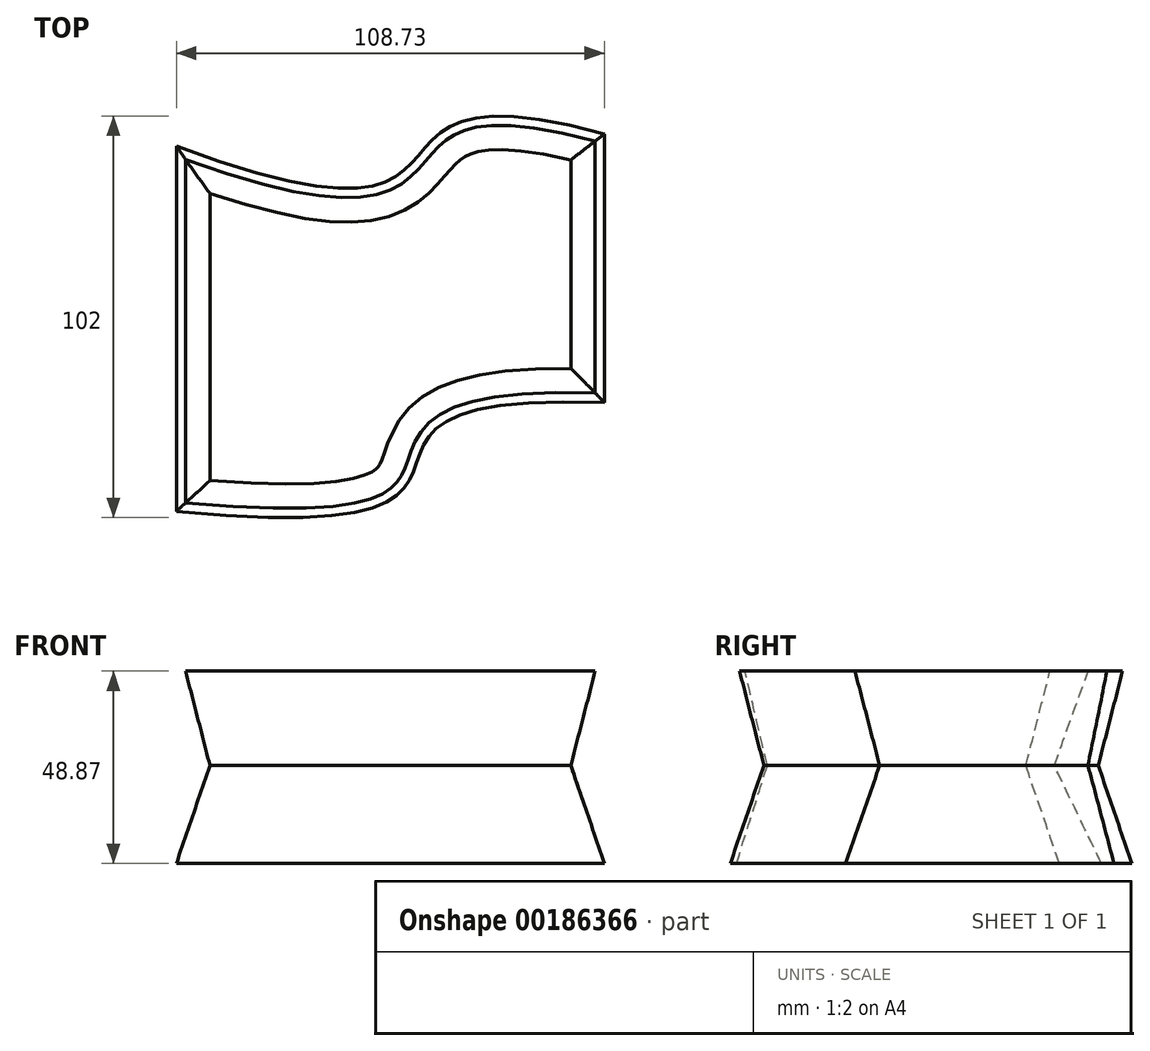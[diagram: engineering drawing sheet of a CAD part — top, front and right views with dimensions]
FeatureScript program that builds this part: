
annotation { "Feature Type Name" : "Feature", "Feature Type Description" : "" }
export const myFeature = defineFeature(function(context is Context, id is Id, definition is map)
    precondition{}
    {
        {
            var Q0;
            Q0=qCreatedBy(makeId("Top.planeOp"),FACE);
            var sketch = newSketch(context, id + "F0", { "sketchPlane" : qUnion([Q0])});
            skLineSegment(sketch, "E0", {"start": v(62.62, 42.09) * mm, "end": v(62.62, -26.14) * mm});
            skLineSegment(sketch, "E1", {"start": v(-46.11, 38.97) * mm, "end": v(-46.11, 0) * mm});
            skFitSpline(sketch, "E2", {"points": [v(62.62, 42.09) * mm, v(-46.11, 38.97) * mm], "startDerivative": vector(-221.63, 61.3) * mm, "endDerivative": vector(-271.64, 100.05) * mm});
            skFitSpline(sketch, "E3", {"points": [v(62.62, -26.14) * mm, v(-46.11, -53.77) * mm], "startDerivative": vector(-264.1, 9.7) * mm, "endDerivative": vector(-314.42, 30.05) * mm});
            skLineSegment(sketch, "E4", {"start": v(-46.11, 0) * mm, "end": v(-46.11, -53.77) * mm});
            skSolve(sketch);
        }
        {
            var Q0;
            Q0=qCreatedBy(makeId("Front.planeOp"),FACE);
            var sketch = newSketch(context, id + "F1", { "sketchPlane" : qUnion([Q0])});
            skLineSegment(sketch, "E5", {"start": v(-46.11, 0) * mm, "end": v(0, 0) * mm});
            skLineSegment(sketch, "E6", {"start": v(0, 0) * mm, "end": v(0, 48.87) * mm});
            skLineSegment(sketch, "E7", {"start": v(0, 48.87) * mm, "end": v(-43.77, 48.87) * mm});
            skLineSegment(sketch, "E8", {"start": v(-43.77, 48.87) * mm, "end": v(-37.59, 24.89) * mm});
            skLineSegment(sketch, "E9", {"start": v(-37.59, 24.89) * mm, "end": v(-46.11, 0) * mm});
            skSolve(sketch);
        }
        {
            var Q0;
            Q0 = qSketchRegion(id + "F1", true);
            var Q1;
            Q1=sQuery(id+"F1.wireOp",EDGE,"E8");
            var Q2;
            Q2=sQuery(id+"F1.wireOp",EDGE,"E9");
            var Q3;
            Q3 = qConstructionFilter(qBodyType(qCreatedBy(id + "F0" ,EDGE), BodyType.WIRE), ConstructionObject.NO);
            sweep(context, id + "F2", {"bodyType" : ExtendedToolBodyType.SURFACE, "profiles" : qUnion([Q0]), "surfaceProfiles" : qUnion([Q1, Q2]), "path" : qUnion([Q3])});
        }
    });
